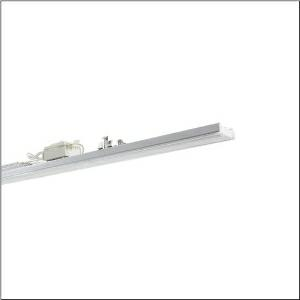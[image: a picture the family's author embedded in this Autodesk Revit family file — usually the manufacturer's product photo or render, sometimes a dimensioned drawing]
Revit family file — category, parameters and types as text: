
# Revit family: licross_21_recessed_mo_51te11vn445g
name_source: partatom
category: Lighting Fixtures
units: mm (PartAtom-declared; Revit-internal decimal feet)

## family parameters
Cut with Voids When Loaded = No
Host = Face
Light Source = No
Part Type = Normal
Room Calculation Point = No
Round Connector Dimension = Use Diameter
Shared = No

## types (1)
- --- (1 x LED, 4500 lm, 24.3 W, 4000K)
    Apparent Load = 24 VA
    CIE Flux Codes = 89 96 99 100 100
    Color Rendering = 80
    Color Temperature = 4000K
    Default Elevation = 1800 mm
    Description = Licross 21 Recessed MO, luminaire insert, of sheet steel, galvanised, coil coated, white, length: 1.500mm, width: 66mm, height: 67mm, LED rated luminous flux: 4.500lm, light colour: 840, SDCM (Standard Deviation of Colour Matching)MacAdam ≤ 2 SDCM (initial), control gear: DALI 2, CLO, with plug, 5-pole, with phase selection, mains connection: 220..240V, AC, 50/60Hz, start of lifetime: 24W, end of service life: 26W, internal wiring halogen-free, primary light control with lens, of plastic, primary optical cover: cover, of PMMA, light emission: direct distribution, primary light characteristic: symmetric, protection rating (complete): IP54, insulation class (complete): insulation class I (protective earthing), certification: CE, ENEC, VDE, UKCA, protection symbol: D if used in an environment with non-conductive dust loads with corresponding accessories, impact resistance: IK06, permissible ambient temperature for indoor applications: -25..+45°C, corresponds to IFS (International Featured Standards) requirements for safety and quality in the food industry, reducing of maximum allowable ambient temperature of 5°C with ceiling mounting, LABS conformity tested according to VDMA 24364:2018-05, The light source and the operating device comply with the requirements of the Ecodesign Regulation (EU) 2019/2020 and are replaceable in accordance with this regulation, packaging unit: 1 piece
    Height = 58 mm
    Lamp = 1 x LED
    Lamp Light Flux = 4500 lm
    Lamp Power = 24.3 W
    Lamp count = 1
    Length = 1500 mm
    Luminous efficacy = 185 lm/W
    Manufacturer = Siteco
    ModVariant = No
    Model = 51TE11VN445G
    Mounting Place = Ceiling
    Mounting Type = Pendant
    Number of Poles = 1
    OnlyDefault = Yes
    Power Factor = 1
    Product Name = Licross 21 Recessed MO
    Product group = luminaire insert | ceiling pendant
    ProductGroupID = 901
    Protection Class = Protection class I
    Protection Degree = IP 54
    RLX_Detail_Level = 1
    RLX_Emergency_Light_Flux = 0 lm
    RLX_Emergency_Type = 0
    RLX_Emergency_Type_DB = No
    RlxData = <blob elided: 24509 chars, md5=8f0bc1a2>
    Socket = socket
    Standby Power = 0 W
    System Light Flux = 4500 lm
    System Power = 24 W
    Type Comments = factory setting: luminous flux: 100 % | dim-lin: 254 | 160 mA
    Type Image = l_1296930.jpg
    URL = http://relux.com
    VarID = @adj_092319
    Voltage = 0 V
    Weight = 0.00 kg
    Width = 66 mm

## geometry (parser evidence)
native form markers: Blend x4, Sweep x11
no freeform markers — native parametric forms only
